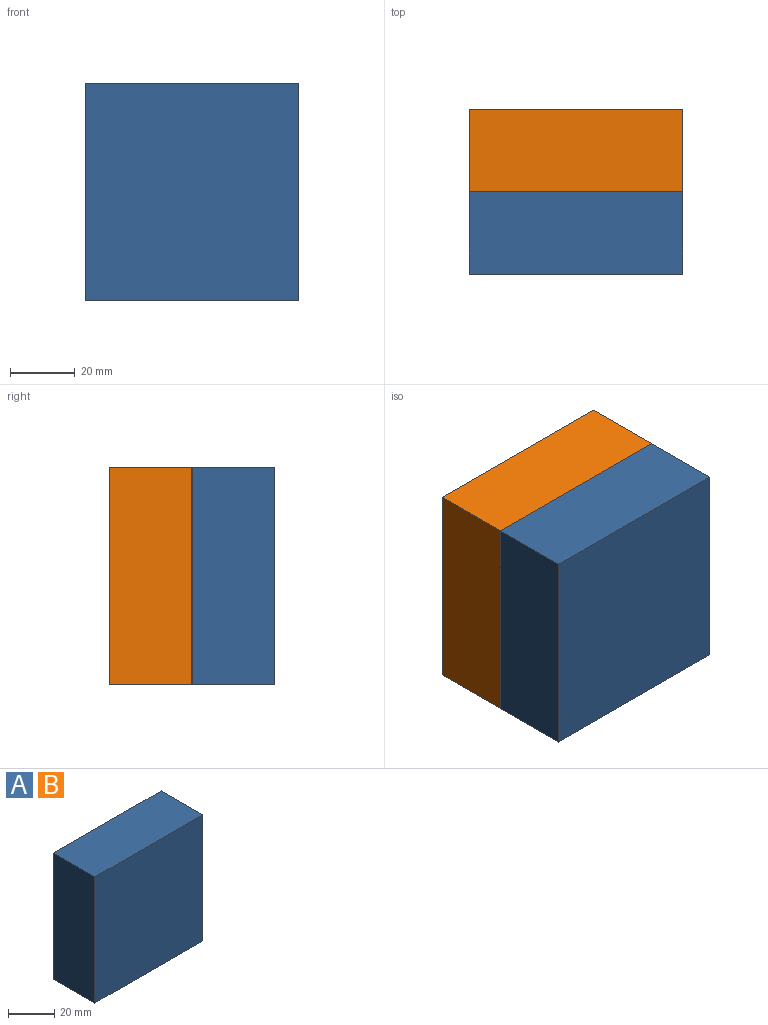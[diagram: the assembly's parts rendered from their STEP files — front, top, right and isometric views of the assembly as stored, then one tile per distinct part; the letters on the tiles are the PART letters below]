
ASSEMBLY  parts=2 mates=1
PART A: 6 faces, bbox 66x25.4x67.1 mm
  f0: plane 67.14x25.4mm, normal (-1,0,0), area 1705.5mm2, adj f1,f3,f4,f5
  f1: plane 66.05x25.4mm, normal (0,0,-1), area 1677.6mm2, adj f0,f2,f4,f5
  f2: plane 67.14x25.4mm, normal (1,0,0), area 1705.5mm2, adj f1,f3,f4,f5
  f3: plane 66.05x25.4mm, normal (0,0,1), area 1677.6mm2, adj f0,f2,f4,f5
  f4: plane 67.14x66.05mm, normal (0,-1,0), area 4434.6mm2, adj f0,f1,f2,f3
  f5: plane 67.14x66.05mm, normal (0,1,0), area 4434.6mm2, adj f0,f1,f2,f3
PART B: same geometry as A
PLACE A rot(axis=(1,0,0),180deg) t=(87.07,-39.63,5.54)mm
PLACE B t=(87.07,11.17,-4.07)mm
MATE fastened A.f4 <-> B.f4  axis (0,1,0) through (4.51,-14.23,0.73)mm
